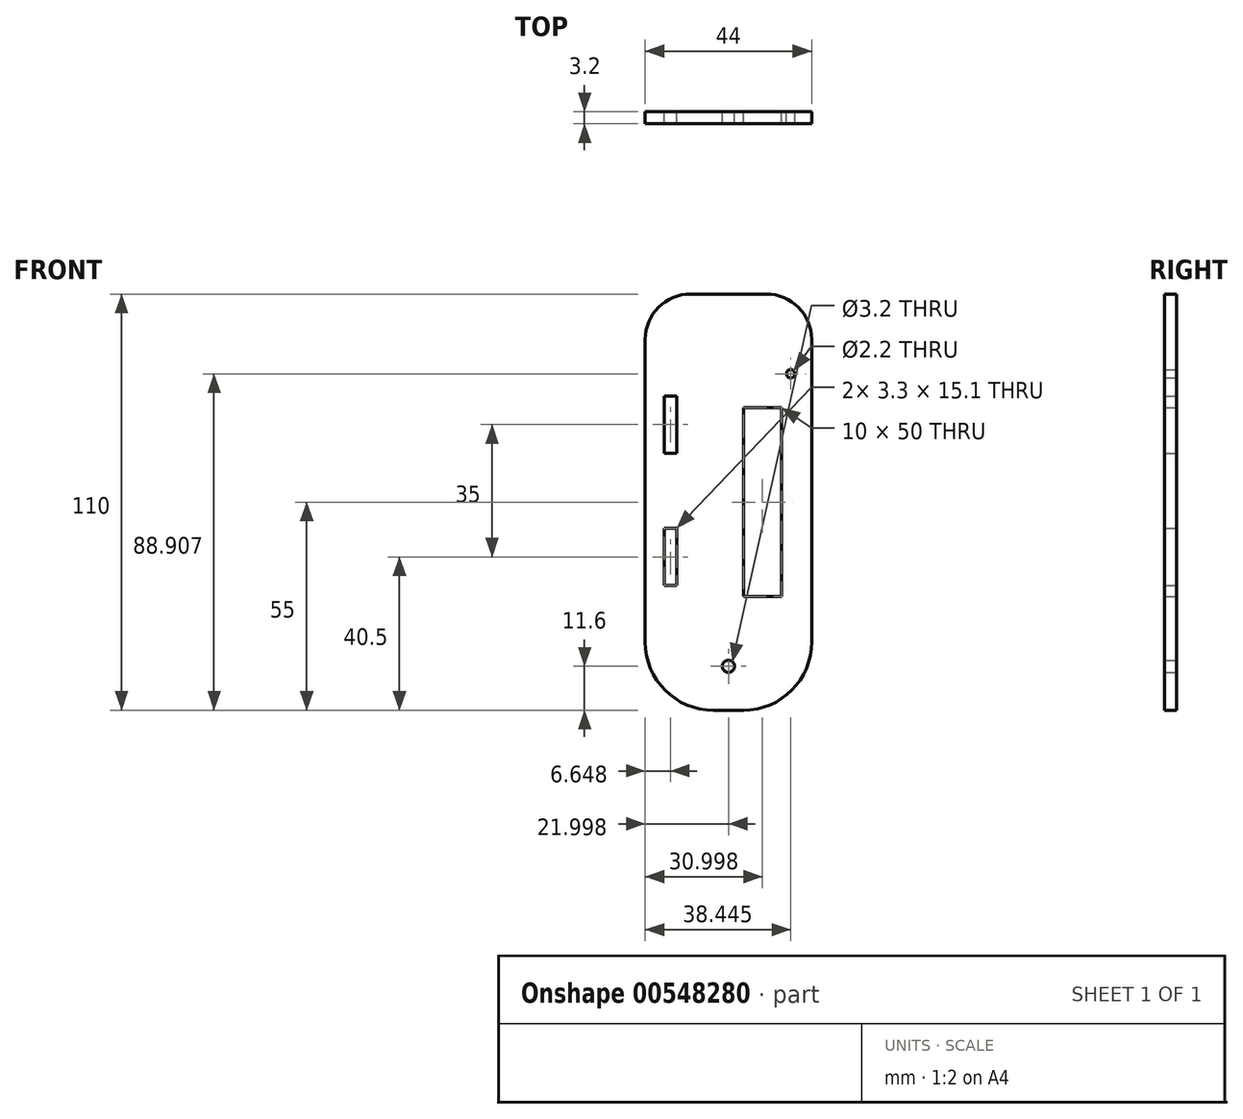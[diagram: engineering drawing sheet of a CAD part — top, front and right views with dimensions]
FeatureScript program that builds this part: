
annotation { "Feature Type Name" : "Feature", "Feature Type Description" : "" }
export const myFeature = defineFeature(function(context is Context, id is Id, definition is map)
    precondition{}
    {
        {
            var Q0;
            Q0=qCreatedBy(makeId("Front.planeOp"),FACE);
            var sketch = newSketch(context, id + "F0", { "sketchPlane" : qUnion([Q0])});
            skLineSegment(sketch, "E0.bottom", {"start": v(-2.9, 110) * mm, "end": v(17.1, 110) * mm});
            skLineSegment(sketch, "E0.top", {"start": v(3.1, 0) * mm, "end": v(11.1, 0) * mm});
            skLineSegment(sketch, "E0.left", {"start": v(-14.9, 98) * mm, "end": v(-14.9, 18) * mm});
            skLineSegment(sketch, "E0.right", {"start": v(29.1, 98) * mm, "end": v(29.1, 18) * mm});
            skPoint(sketch, "E1.visualSharp", {"position": v(-14.9, 110) * mm});
            skArc(sketch, "E1.filletArc", {"start": v(-2.9, 110) * mm, "mid": v(-11.38, 106.49) * mm, "end": v(-14.9, 98) * mm});
            skPoint(sketch, "E2.visualSharp", {"position": v(29.1, 110) * mm});
            skArc(sketch, "E2.filletArc", {"start": v(29.1, 98) * mm, "mid": v(25.6, 106.49) * mm, "end": v(17.1, 110) * mm});
            skPoint(sketch, "E3.visualSharp", {"position": v(-14.9, 0) * mm});
            skArc(sketch, "E3.filletArc", {"start": v(-14.9, 18) * mm, "mid": v(-9.62, 5.27) * mm, "end": v(3.1, 0) * mm});
            skPoint(sketch, "E4.visualSharp", {"position": v(29.1, 0) * mm});
            skArc(sketch, "E4.filletArc", {"start": v(11.1, 0) * mm, "mid": v(23.84, 5.27) * mm, "end": v(29.1, 18) * mm});
            skCircle(sketch, "E5", {"center": v(7.1, 11.6) * mm, "radius": 1.6 * mm});
            skLineSegment(sketch, "E6.bottom", {"start": v(-9.9, 32.95) * mm, "end": v(-6.6, 32.95) * mm});
            skLineSegment(sketch, "E6.top", {"start": v(-9.9, 48.05) * mm, "end": v(-6.6, 48.05) * mm});
            skLineSegment(sketch, "E6.left", {"start": v(-9.9, 32.95) * mm, "end": v(-9.9, 48.05) * mm});
            skLineSegment(sketch, "E6.right", {"start": v(-6.6, 32.95) * mm, "end": v(-6.6, 48.05) * mm});
            skLineSegment(sketch, "E7.bottom", {"start": v(-9.9, 67.95) * mm, "end": v(-6.6, 67.95) * mm});
            skLineSegment(sketch, "E7.top", {"start": v(-9.9, 83.05) * mm, "end": v(-6.6, 83.05) * mm});
            skLineSegment(sketch, "E7.left", {"start": v(-9.9, 67.95) * mm, "end": v(-9.9, 83.05) * mm});
            skLineSegment(sketch, "E7.right", {"start": v(-6.6, 67.95) * mm, "end": v(-6.6, 83.05) * mm});
            skLineSegment(sketch, "E8.bottom", {"start": v(11.1, 30) * mm, "end": v(21.1, 30) * mm});
            skLineSegment(sketch, "E8.top", {"start": v(11.1, 80) * mm, "end": v(21.1, 80) * mm});
            skLineSegment(sketch, "E8.left", {"start": v(11.1, 30) * mm, "end": v(11.1, 80) * mm});
            skLineSegment(sketch, "E8.right", {"start": v(21.1, 30) * mm, "end": v(21.1, 80) * mm});
            skCircle(sketch, "E9", {"center": v(23.56, 88.9) * mm, "radius": 1.1 * mm});
            skSolve(sketch);
        }
        {
            var Q0;
            Q0=qSketchRegion(id+"F0",true);
            extrude(context, id + "F1", {"entities" : qUnion([Q0]), "depth" : 3.2 * mm, "offsetDistance" : 25 * mm});
        }
    });
